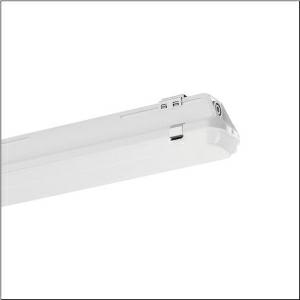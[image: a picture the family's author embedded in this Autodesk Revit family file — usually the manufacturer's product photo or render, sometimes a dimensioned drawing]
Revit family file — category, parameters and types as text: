
# Revit family: monsun_r__11_51fp12dp4b0u_6f6f
name_source: partatom
category: Lighting Fixtures
units: mm (PartAtom-declared; Revit-internal decimal feet)

## family parameters
Cut with Voids When Loaded = No
Host = Face
Light Source = No
Part Type = Normal
Room Calculation Point = No
Round Connector Dimension = Use Diameter
Shared = No

## types (1)
- --- (1 x LED, 11850 lm, 63.5 W, 4000K)
    Apparent Load = 64 VA
    CIE Flux Codes = 62 86 96 97 100
    Color Rendering = 80
    Color Temperature = 4000K
    Default Elevation = 1800 mm
    Description = Monsun® 11, damp-proof luminaire, chain hanger, primary light control with lens, primary optical cover: enclosure, of PMMA, light emission: direct distribution, primary light characteristic: symmetric, installation type: suspended mounting, surface-mounted, horizontal mounting, vertical mounting, LED, rated luminous flux: 11.850lm, luminous efficacy: 187lm/W, light colour: 840, colour temperature: 4000K, control gear: DALI 2, with terminal, 5-pole, max. 2.5mm², mains connection: 220..240V, AC, 50/60Hz, rated input power: 64W, luminaire housing, of glass-fibre reinforced polyester, uncoated, bright grey, incl. chain hanger, length: 1.590mm, width: 90mm, height: 88mm, clip for enclosure, of stainless steel (V2A), ceiling mounting element, of stainless steel (V2A), chain hanger, of stainless steel (V2A), protection rating (complete): IP66, insulation class (complete): insulation class I (protective earthing), certification: CE, ENEC, VDE, UKCA, protection symbol: D, impact resistance: IK04, permissible operating ambient temperature: -35..+35°C, standard: EN 50419, EN 60598-2-1, corresponds to IFS (International Featured Standards) requirements for safety and quality in the food industry, for indoor or canopied outdoor use, no direct snow, no direct sun, no direct rain, LABS conformity tested according to VDMA 24364:2018-05, contact your sales advisor before using the luminaires in applications with unclear chemical exposure, large temperature fluctuations or condensation-forming humidity, packaging unit: 1 piece
    Height = 89 mm
    Lamp = 1 x LED
    Lamp Light Flux = 11850 lm
    Lamp Power = 63.5 W
    Lamp count = 1
    Length = 1590 mm
    Luminous efficacy = 187 lm/W
    Manufacturer = Siteco
    ModVariant = No
    Model = 51FP12DP4B0U
    Mounting Place = Ceiling
    Mounting Type = Surface mounted
    Number of Poles = 1
    OnlyDefault = Yes
    Power Factor = 1
    Product Name = Monsun® 11
    Product group = damp-proof luminaire
    ProductGroupID = 300
    Protection Class = Protection class I
    Protection Degree = IP 66
    RLX_Detail_Level = 1
    RLX_Emergency_Light_Flux = 0 lm
    RLX_Emergency_Type = 0
    RLX_Emergency_Type_DB = No
    RlxData = <blob elided: 92569 chars, md5=930e39bc>
    Socket = socket
    Standby Power = 0 W
    System Light Flux = 11850 lm
    System Power = 64 W
    Type Comments = factory setting: luminous flux: 100 % | dim-lin: 254 | 439 mA
    Type Image = l_1349237.jpg
    URL = http://relux.com
    VarID = @adj_023034
    Voltage = 0 V
    Weight = 0.00 kg
    Width = 90 mm

## geometry (parser evidence)
native form markers: Blend x4, Sweep x11
no freeform markers — native parametric forms only
